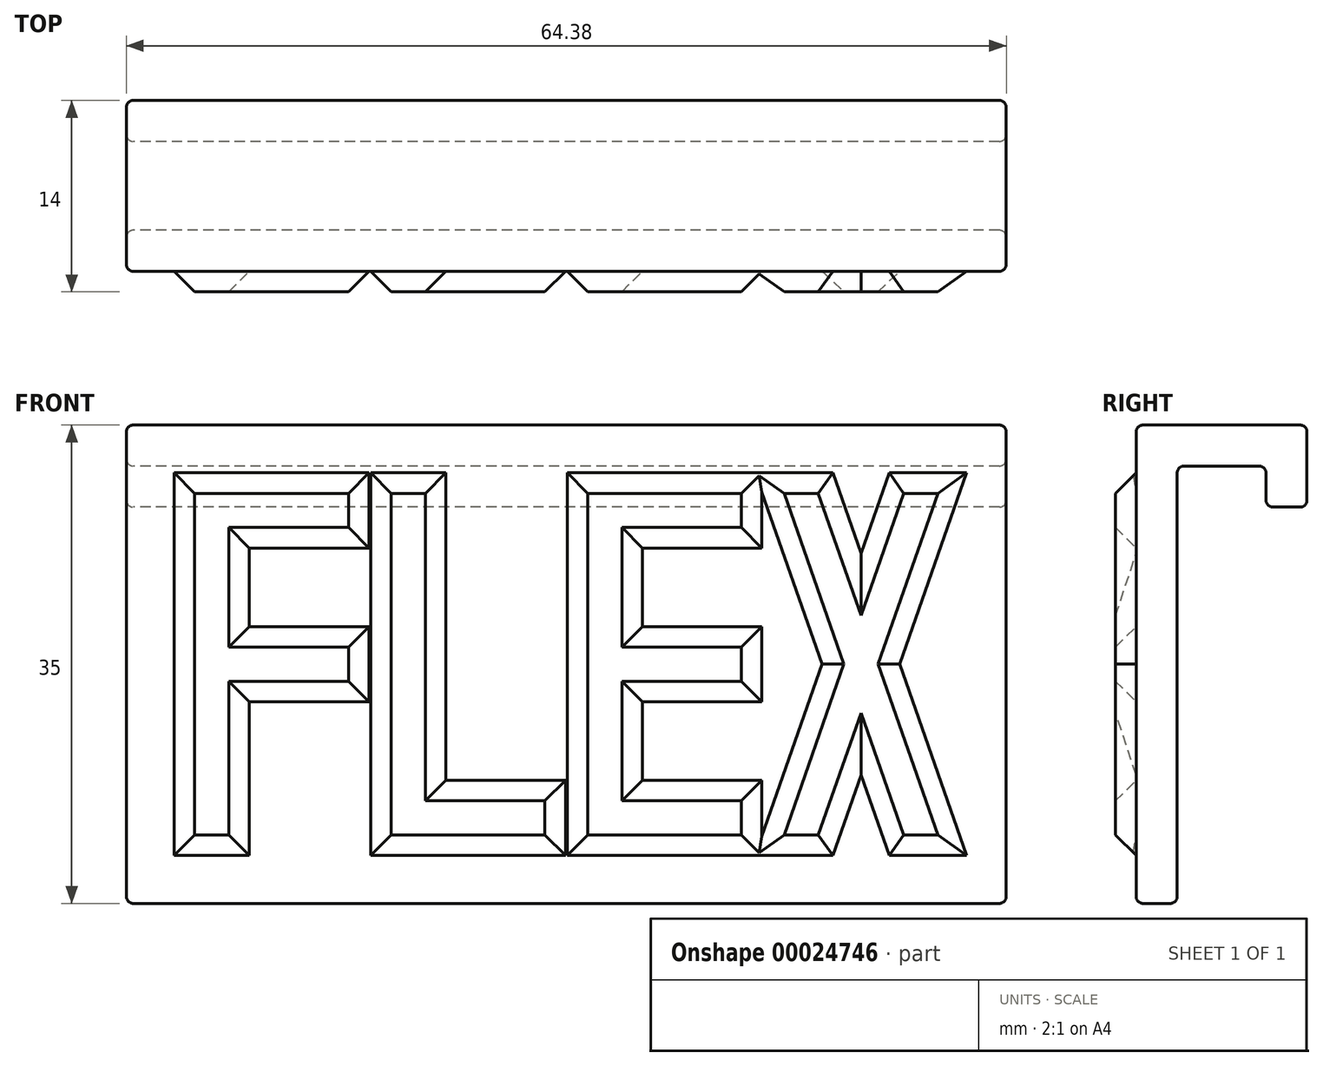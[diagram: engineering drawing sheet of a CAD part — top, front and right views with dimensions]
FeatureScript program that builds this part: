
annotation { "Feature Type Name" : "Feature", "Feature Type Description" : "" }
export const myFeature = defineFeature(function(context is Context, id is Id, definition is map)
    precondition{}
    {
        {
            var Q0;
            Q0=qCreatedBy(makeId("Right.planeOp"),FACE);
            var sketch = newSketch(context, id + "F0", { "sketchPlane" : qUnion([Q0])});
            skLineSegment(sketch, "E0", {"start": v(0, 0) * mm, "end": v(0, 35) * mm});
            skLineSegment(sketch, "E1", {"start": v(0, 35) * mm, "end": v(12.5, 35) * mm});
            skLineSegment(sketch, "E2", {"start": v(12.5, 35) * mm, "end": v(12.5, 29) * mm});
            skLineSegment(sketch, "E3", {"start": v(12.5, 29) * mm, "end": v(9.5, 29) * mm});
            skLineSegment(sketch, "E4", {"start": v(9.5, 29) * mm, "end": v(9.5, 32) * mm});
            skLineSegment(sketch, "E5", {"start": v(9.5, 32) * mm, "end": v(3, 32) * mm});
            skLineSegment(sketch, "E6", {"start": v(3, 32) * mm, "end": v(3, 0) * mm});
            skLineSegment(sketch, "E7", {"start": v(3, 0) * mm, "end": v(0, 0) * mm});
            skSolve(sketch);
        }
        {
            var Q0;
            Q0=qSketchRegion(id+"F0",true);
            extrude(context, id + "F1", {"entities" : qUnion([Q0]), "depth" : 64.38 * mm});
        }
        {
            var Q0;
            Q0=makeQuery(id+"F1.opExtrude","SWEPT_FACE",FACE,{"disambiguationData":[OSD([sQuery(id+"F0.wireOp",EDGE,"E0")])]});
            var sketch = newSketch(context, id + "F2", { "sketchPlane" : qUnion([Q0])});
            skLineSegment(sketch, "E8", {"start": v(31.88, 35) * mm, "end": v(31.88, 0) * mm});
            skLineSegment(sketch, "E9", {"start": v(46.88, 35) * mm, "end": v(46.88, 0) * mm});
            skLineSegment(sketch, "E10", {"start": v(0, 5) * mm, "end": v(64.38, 5) * mm});
            skLineSegment(sketch, "E11", {"start": v(2.5, 35) * mm, "end": v(2.5, 0) * mm});
            skLineSegment(sketch, "E12", {"start": v(61.88, 35) * mm, "end": v(61.88, 0) * mm});
            skPoint(sketch, "E13", {"position": v(61.88, 30) * mm});
            skPoint(sketch, "E14", {"position": v(61.88, 5) * mm});
            skPoint(sketch, "E15.trimOffspring.end.orphan", {"position": v(0, 30) * mm});
            skLineSegment(sketch, "E16", {"start": v(2.5, 35) * mm, "end": v(17.5, 35) * mm});
            skLineSegment(sketch, "E17", {"start": v(17.5, 35) * mm, "end": v(17.5, 0) * mm});
            skLineSegment(sketch, "E18", {"start": v(0, 30) * mm, "end": v(64.38, 30) * mm});
            skLineSegment(sketch, "E19", {"start": v(2.5, 30) * mm, "end": v(5, 30) * mm});
            skLineSegment(sketch, "E20", {"start": v(5, 30) * mm, "end": v(5, 5) * mm});
            skLineSegment(sketch, "E21", {"start": v(17.5, 30) * mm, "end": v(16.25, 30) * mm});
            skLineSegment(sketch, "E22", {"start": v(16.25, 30) * mm, "end": v(16.25, 27.5) * mm});
            skLineSegment(sketch, "E23", {"start": v(7.5, 27.5) * mm, "end": v(16.25, 27.5) * mm});
            skLineSegment(sketch, "E24", {"start": v(16.25, 27.5) * mm, "end": v(16.25, 30) * mm});
            skLineSegment(sketch, "E25", {"start": v(7.5, 27.5) * mm, "end": v(7.5, 18.75) * mm});
            skLineSegment(sketch, "E26", {"start": v(7.5, 18.75) * mm, "end": v(16.25, 18.75) * mm});
            skLineSegment(sketch, "E27", {"start": v(16.25, 18.75) * mm, "end": v(16.25, 16.25) * mm});
            skLineSegment(sketch, "E28", {"start": v(16.25, 16.25) * mm, "end": v(7.5, 16.25) * mm});
            skLineSegment(sketch, "E29.trimOffspring", {"start": v(7.5, 16.25) * mm, "end": v(7.5, 5) * mm});
            skPoint(sketch, "E30.start.orphan", {"position": v(5, 17.5) * mm});
            skPoint(sketch, "E31.orphan", {"position": v(7.5, 17.5) * mm});
            skLineSegment(sketch, "E32", {"start": v(17.5, 30) * mm, "end": v(19.38, 30) * mm});
            skLineSegment(sketch, "E33", {"start": v(19.38, 30) * mm, "end": v(19.38, 5) * mm});
            skLineSegment(sketch, "E34", {"start": v(19.38, 30) * mm, "end": v(21.88, 30) * mm});
            skLineSegment(sketch, "E35", {"start": v(21.88, 30) * mm, "end": v(21.88, 7.5) * mm});
            skLineSegment(sketch, "E36", {"start": v(31.88, 5) * mm, "end": v(30.62, 5) * mm});
            skLineSegment(sketch, "E37", {"start": v(21.88, 7.5) * mm, "end": v(30.62, 7.5) * mm});
            skLineSegment(sketch, "E38", {"start": v(30.62, 7.5) * mm, "end": v(30.62, 5) * mm});
            skLineSegment(sketch, "E39", {"start": v(31.88, 30) * mm, "end": v(33.75, 30) * mm});
            skLineSegment(sketch, "E40", {"start": v(33.75, 30) * mm, "end": v(33.75, 5) * mm});
            skLineSegment(sketch, "E41", {"start": v(46.88, 5) * mm, "end": v(45, 5) * mm});
            skLineSegment(sketch, "E42", {"start": v(45, 5) * mm, "end": v(33.75, 5) * mm});
            skLineSegment(sketch, "E43", {"start": v(33.75, 30) * mm, "end": v(45, 30) * mm});
            skLineSegment(sketch, "E44", {"start": v(45, 30) * mm, "end": v(45, 27.5) * mm});
            skLineSegment(sketch, "E45", {"start": v(45, 27.5) * mm, "end": v(36.25, 27.5) * mm});
            skLineSegment(sketch, "E46", {"start": v(36.25, 27.5) * mm, "end": v(36.25, 18.75) * mm});
            skLineSegment(sketch, "E47", {"start": v(36.25, 18.75) * mm, "end": v(45, 18.75) * mm});
            skLineSegment(sketch, "E48", {"start": v(45, 18.75) * mm, "end": v(45, 16.25) * mm});
            skLineSegment(sketch, "E49", {"start": v(45, 16.25) * mm, "end": v(36.25, 16.25) * mm});
            skLineSegment(sketch, "E50", {"start": v(36.25, 16.25) * mm, "end": v(36.25, 7.5) * mm});
            skLineSegment(sketch, "E51", {"start": v(36.25, 7.5) * mm, "end": v(45, 7.5) * mm});
            skLineSegment(sketch, "E52", {"start": v(45, 7.5) * mm, "end": v(45, 5) * mm});
            skLineSegment(sketch, "E53", {"start": v(46.88, 30) * mm, "end": v(48.12, 30) * mm});
            skLineSegment(sketch, "E54", {"start": v(61.88, 5) * mm, "end": v(59.38, 5) * mm});
            skLineSegment(sketch, "E55", {"start": v(48.12, 30) * mm, "end": v(50.62, 30) * mm});
            skLineSegment(sketch, "E56", {"start": v(59.38, 5) * mm, "end": v(56.87, 5) * mm});
            skLineSegment(sketch, "E57", {"start": v(46.88, 5) * mm, "end": v(53.8, 5) * mm});
            skLineSegment(sketch, "E58", {"start": v(59.38, 5) * mm, "end": v(48.12, 5) * mm});
            skLineSegment(sketch, "E59", {"start": v(48.12, 30) * mm, "end": v(52.5, 17.5) * mm});
            skLineSegment(sketch, "E60", {"start": v(50.62, 30) * mm, "end": v(53.75, 21.07) * mm});
            skLineSegment(sketch, "E61", {"start": v(59.38, 30) * mm, "end": v(55, 17.5) * mm});
            skLineSegment(sketch, "E62", {"start": v(48.12, 5) * mm, "end": v(52.5, 17.5) * mm});
            skLineSegment(sketch, "E63.trimOffspring", {"start": v(53.75, 21.07) * mm, "end": v(56.87, 30) * mm});
            skLineSegment(sketch, "E64.trimOffspring", {"start": v(55, 17.5) * mm, "end": v(59.38, 5) * mm});
            skLineSegment(sketch, "E65.trimOffspring", {"start": v(53.75, 13.93) * mm, "end": v(56.87, 5) * mm});
            skLineSegment(sketch, "E66.trimOffspring", {"start": v(53.75, 13.93) * mm, "end": v(50.62, 5) * mm});
            skLineSegment(sketch, "E67", {"start": v(48.12, 30) * mm, "end": v(48.12, 5) * mm});
            skLineSegment(sketch, "E68", {"start": v(59.38, 30) * mm, "end": v(59.38, 5) * mm});
            skSolve(sketch);
        }
        {
            var Q0;
            {var subQ2=sQuery(id+"F2.wireOp",EDGE,"E20");Q0=makeQuery(id+"F2.imprint","IMPRINT",FACE,{"disambiguationData":[TD([[makeQuery(id+"F2.imprint","IMPRINT",EDGE,{"derivedFrom":subQ2}),1.0]])]});}
            var Q1;
            {var subQ1=sQuery(id+"F2.wireOp",EDGE,"E33");Q1=makeQuery(id+"F2.imprint","IMPRINT",FACE,{"disambiguationData":[TD([[makeQuery(id+"F2.imprint","IMPRINT",EDGE,{"derivedFrom":subQ1}),1.0]])]});}
            var Q2;
            Q2=makeQuery(id+"F2.imprint","IMPRINT",FACE,{"disambiguationData":[TD([[makeQuery(id+"F2.imprint","IMPRINT",EDGE,{"derivedFrom":sQuery(id+"F2.wireOp",EDGE,"E40")}),1.0]])]});
            var Q3;
            {var subQ7=sQuery(id+"F2.wireOp",EDGE,"E62");var subQ17=sQuery(id+"F2.wireOp",EDGE,"E59");var subQ21=makeQuery(id+"F2.imprint","INTERSECT",VERTEX,{"derivedFrom":[subQ17,subQ7]});Q3=makeQuery(id+"F2.imprint","IMPRINT",FACE,{"disambiguationData":[TD([[makeQuery(id+"F2.imprint","IMPRINT",EDGE,{"disambiguationData":[TD([[subQ21,1.0]])],"derivedFrom":subQ17}),1.0]])]});}
            extrude(context, id + "F3", {"entities" : qUnion([Q0, Q1, Q2, Q3]), "operationType" : NewBodyOperationType.ADD, "depth" : 1.5 * mm});
        }
        {
            var Q0;
            Q0=makeQuery(id+"F1.opExtrude","CAP_FACE",FACE,{"disambiguationData":[OSD([sQuery(id+"F0.wireOp",EDGE,"E0"),sQuery(id+"F0.wireOp",EDGE,"E1"),sQuery(id+"F0.wireOp",EDGE,"E2"),sQuery(id+"F0.wireOp",EDGE,"E3"),sQuery(id+"F0.wireOp",EDGE,"E4"),sQuery(id+"F0.wireOp",EDGE,"E5"),sQuery(id+"F0.wireOp",EDGE,"E6"),sQuery(id+"F0.wireOp",EDGE,"E7")])],"isStart":true});
            var Q1;
            Q1=makeQuery(id+"F1.opExtrude","SWEPT_FACE",FACE,{"disambiguationData":[OSD([sQuery(id+"F0.wireOp",EDGE,"E6")])]});
            var Q2;
            Q2=makeQuery(id+"F1.opExtrude","SWEPT_FACE",FACE,{"disambiguationData":[OSD([sQuery(id+"F0.wireOp",EDGE,"E7")])]});
            var Q3;
            Q3=makeQuery(id+"F1.opExtrude","CAP_FACE",FACE,{"disambiguationData":[OSD([sQuery(id+"F0.wireOp",EDGE,"E0"),sQuery(id+"F0.wireOp",EDGE,"E1"),sQuery(id+"F0.wireOp",EDGE,"E2"),sQuery(id+"F0.wireOp",EDGE,"E3"),sQuery(id+"F0.wireOp",EDGE,"E4"),sQuery(id+"F0.wireOp",EDGE,"E5"),sQuery(id+"F0.wireOp",EDGE,"E6"),sQuery(id+"F0.wireOp",EDGE,"E7")])],"isStart":false});
            var Q4;
            Q4=makeQuery(id+"F1.opExtrude","SWEPT_FACE",FACE,{"disambiguationData":[OSD([sQuery(id+"F0.wireOp",EDGE,"E1")])]});
            var Q5;
            Q5=makeQuery(id+"F1.opExtrude","SWEPT_FACE",FACE,{"disambiguationData":[OSD([sQuery(id+"F0.wireOp",EDGE,"E2")])]});
            var Q6;
            Q6=makeQuery(id+"F1.opExtrude","SWEPT_FACE",FACE,{"disambiguationData":[OSD([sQuery(id+"F0.wireOp",EDGE,"E5")])]});
            var Q7;
            Q7=makeQuery(id+"F1.opExtrude","SWEPT_FACE",FACE,{"disambiguationData":[OSD([sQuery(id+"F0.wireOp",EDGE,"E3")])]});
            fillet(context, id + "F4", {"entities" : qUnion([Q0, Q1, Q2, Q3, Q4, Q5, Q6, Q7]), "radius" : .5 * mm, "tangentPropagation" : true, "allowEdgeOverflow" : false});
        }
        {
            var Q0;
            Q0=makeQuery(id+"F1.opExtrude","SWEPT_FACE",FACE,{"disambiguationData":[OSD([sQuery(id+"F0.wireOp",EDGE,"E0")])]});
            chamfer(context, id + "F5", {"entities" : qUnion([Q0]), "width" : 1.5 * mm, "tangentPropagation" : true});
        }
    });
